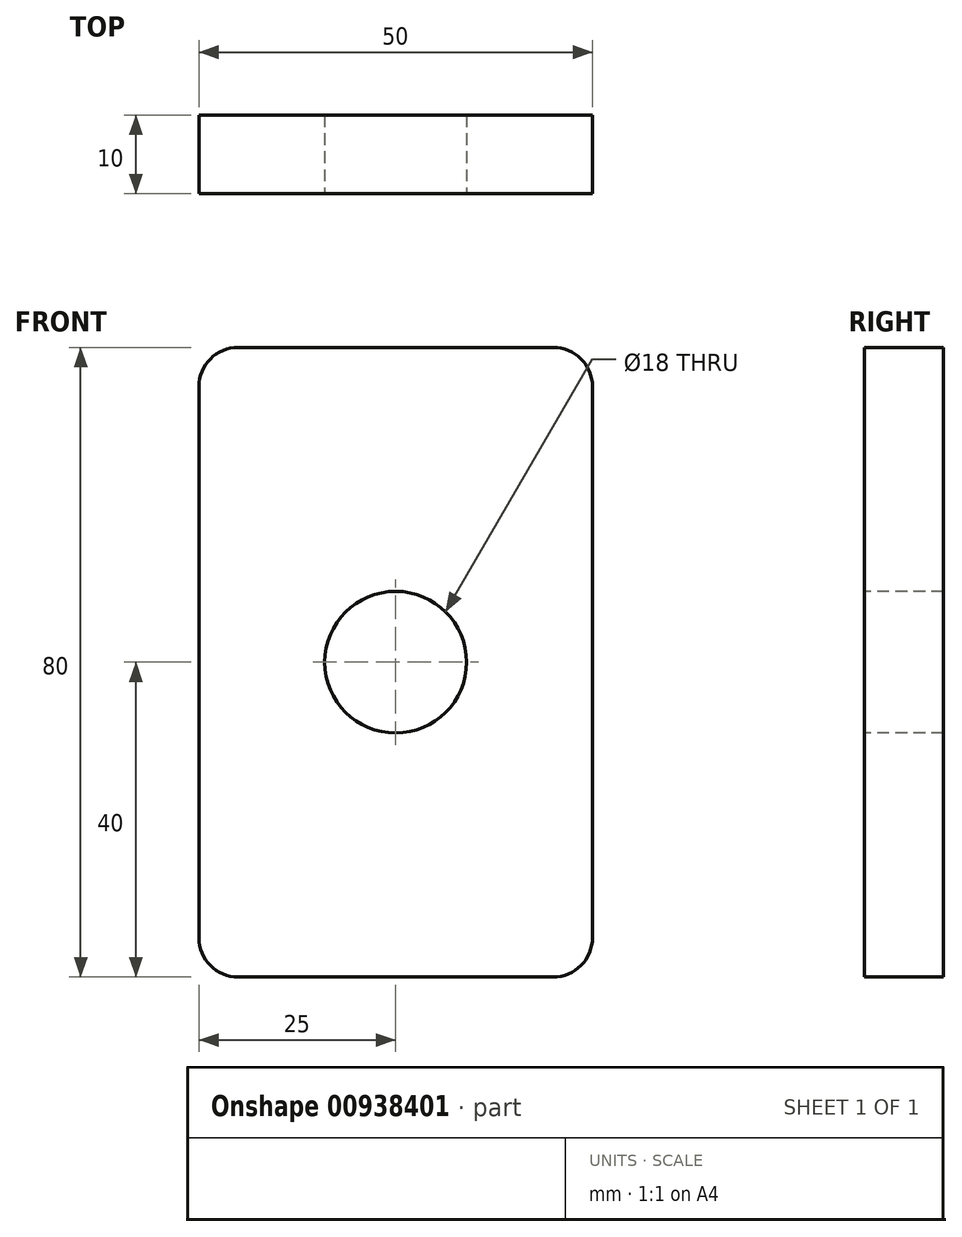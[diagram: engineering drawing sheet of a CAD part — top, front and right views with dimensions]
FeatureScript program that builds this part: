
annotation { "Feature Type Name" : "Feature", "Feature Type Description" : "" }
export const myFeature = defineFeature(function(context is Context, id is Id, definition is map)
    precondition{}
    {
        {
            var Q0;
            Q0=qCreatedBy(makeId("Front.planeOp"),FACE);
            var sketch = newSketch(context, id + "F0", { "sketchPlane" : qUnion([Q0])});
            skLineSegment(sketch, "E0.bottom", {"start": v(0, 0) * mm, "end": v(50, 0) * mm});
            skLineSegment(sketch, "E0.top", {"start": v(0, -80) * mm, "end": v(50, -80) * mm});
            skLineSegment(sketch, "E0.left", {"start": v(0, 0) * mm, "end": v(0, -80) * mm});
            skLineSegment(sketch, "E0.right", {"start": v(50, 0) * mm, "end": v(50, -80) * mm});
            skSolve(sketch);
        }
        {
            var Q0;
            Q0=makeQuery(id+"F0.imprint","IMPRINT",FACE,{"disambiguationData":[TD([[makeQuery(id+"F0.imprint","IMPRINT",EDGE,{"derivedFrom":sQuery(id+"F0.wireOp",EDGE,"E0.bottom")}),-1.0]])]});
            extrude(context, id + "F1", {"entities" : qUnion([Q0]), "depth" : 10 * mm, "offsetDistance" : 25 * mm});
        }
        {
            var Q0;
            Q0=makeQuery(id+"F1.opExtrude","CAP_FACE",FACE,{"disambiguationData":[OSD([sQuery(id+"F0.wireOp",EDGE,"E0.bottom"),sQuery(id+"F0.wireOp",EDGE,"E0.top"),sQuery(id+"F0.wireOp",EDGE,"E0.left"),sQuery(id+"F0.wireOp",EDGE,"E0.right")])],"isStart":false});
            var sketch = newSketch(context, id + "F2", { "sketchPlane" : qUnion([Q0])});
            skCircle(sketch, "E1", {"center": v(25, -40) * mm, "radius": 9 * mm});
            skSolve(sketch);
        }
        {
            var Q0;
            Q0=makeQuery(id+"F2.imprint","IMPRINT",FACE,{"disambiguationData":[TD([[makeQuery(id+"F2.imprint","IMPRINT",EDGE,{"derivedFrom":sQuery(id+"F2.wireOp",EDGE,"E1")}),1.0]])]});
            extrude(context, id + "F3", {"entities" : qUnion([Q0]), "operationType" : NewBodyOperationType.REMOVE, "endBound" : BoundingType.THROUGH_ALL, "oppositeDirection" : true, "depth" : 25 * mm, "offsetDistance" : 25 * mm});
        }
        {
            var Q0;
            Q0=makeQuery(id+"F1.opExtrude","SWEPT_EDGE",EDGE,{"disambiguationData":[OSD([sQuery(id+"F0.wireOp",EDGE,"E0.bottom"),sQuery(id+"F0.wireOp",EDGE,"E0.right")])]});
            var Q1;
            Q1=makeQuery(id+"F1.opExtrude","SWEPT_EDGE",EDGE,{"disambiguationData":[OSD([sQuery(id+"F0.wireOp",EDGE,"E0.bottom"),sQuery(id+"F0.wireOp",EDGE,"E0.left")])]});
            var Q2;
            Q2=makeQuery(id+"F1.opExtrude","SWEPT_EDGE",EDGE,{"disambiguationData":[OSD([sQuery(id+"F0.wireOp",EDGE,"E0.top"),sQuery(id+"F0.wireOp",EDGE,"E0.right")])]});
            var Q3;
            Q3=makeQuery(id+"F1.opExtrude","SWEPT_EDGE",EDGE,{"disambiguationData":[OSD([sQuery(id+"F0.wireOp",EDGE,"E0.top"),sQuery(id+"F0.wireOp",EDGE,"E0.left")])]});
            fillet(context, id + "F4", {"entities" : qUnion([Q0, Q1, Q2, Q3]), "radius" : 5 * mm, "tangentPropagation" : true, "allowEdgeOverflow" : false});
        }
    });
